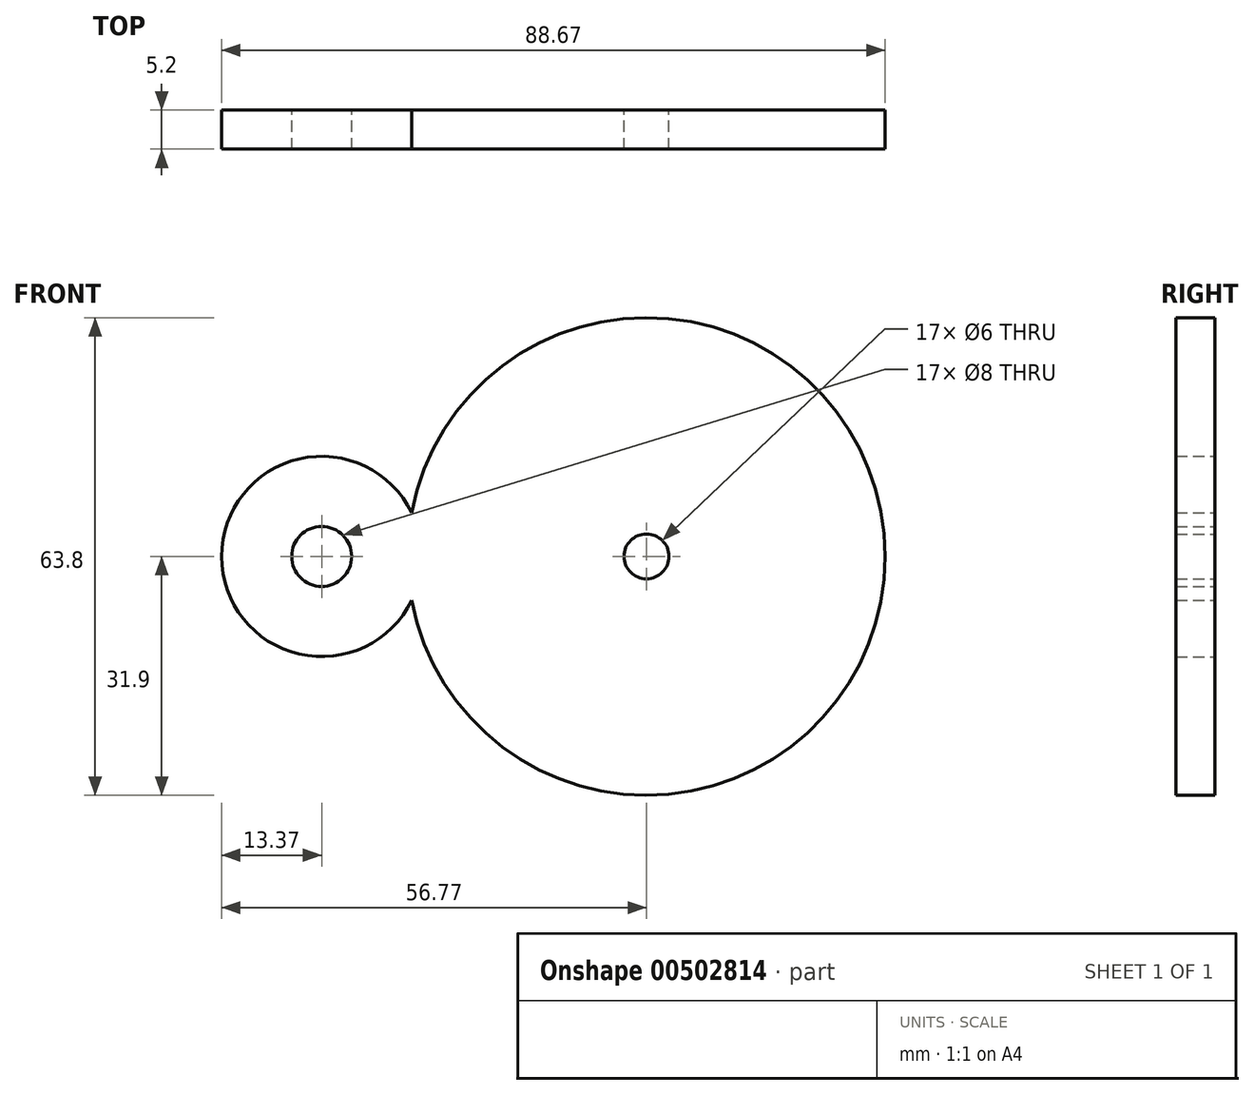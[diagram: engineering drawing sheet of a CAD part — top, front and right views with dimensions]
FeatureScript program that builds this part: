
annotation { "Feature Type Name" : "Feature", "Feature Type Description" : "" }
export const myFeature = defineFeature(function(context is Context, id is Id, definition is map)
    precondition{}
    {
        {
            var Q0;
            Q0=qCreatedBy(makeId("Front.planeOp"),FACE);
            var sketch = newSketch(context, id + "F0", { "sketchPlane" : qUnion([Q0])});
            skCircle(sketch, "E0", {"center": v(0, 0) * mm, "radius": 13.38 * mm});
            skCircle(sketch, "E1", {"center": v(0, 0) * mm, "radius": 4 * mm});
            skCircle(sketch, "E2", {"center": v(43.4, 0) * mm, "radius": 31.9 * mm});
            skCircle(sketch, "E3", {"center": v(43.4, 0) * mm, "radius": 3 * mm});
            skSolve(sketch);
        }
        {
            var Q0;
            Q0=makeQuery(id+"F0.imprint","IMPRINT",FACE,{"disambiguationData":[TD([[makeQuery(id+"F0.imprint","IMPRINT",EDGE,{"derivedFrom":sQuery(id+"F0.wireOp",EDGE,"E0")}),1.0]])]});
            var Q1;
            Q1=makeQuery(id+"F0.imprint","IMPRINT",FACE,{"disambiguationData":[TD([[makeQuery(id+"F0.imprint","IMPRINT",EDGE,{"derivedFrom":sQuery(id+"F0.wireOp",EDGE,"E1")}),-1.0]])]});
            var Q2;
            Q2=makeQuery(id+"F0.imprint","IMPRINT",FACE,{"disambiguationData":[TD([[makeQuery(id+"F0.imprint","IMPRINT",EDGE,{"derivedFrom":sQuery(id+"F0.wireOp",EDGE,"E3")}),-1.0]])]});
            extrude(context, id + "F1", {"entities" : qUnion([Q0, Q1, Q2]), "depth" : 5.2 * mm});
        }
    });
